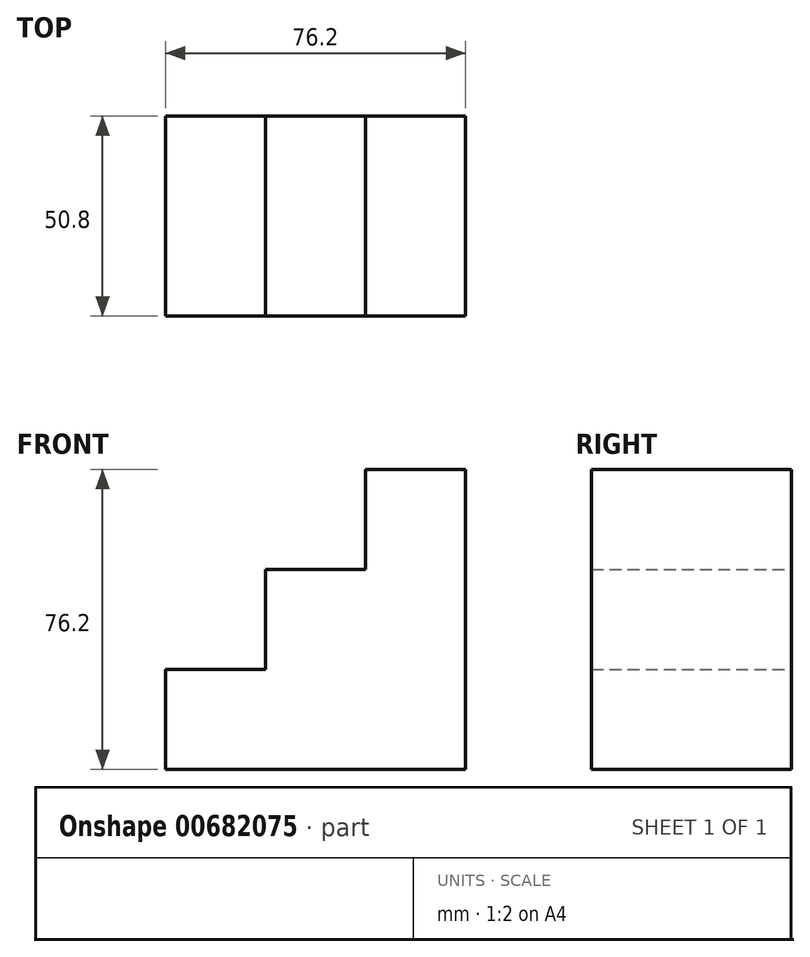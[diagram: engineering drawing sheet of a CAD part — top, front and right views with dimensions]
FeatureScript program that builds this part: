
annotation { "Feature Type Name" : "Feature", "Feature Type Description" : "" }
export const myFeature = defineFeature(function(context is Context, id is Id, definition is map)
    precondition{}
    {
        {
            var Q0;
            Q0=qCreatedBy(makeId("Front.planeOp"),FACE);
            var sketch = newSketch(context, id + "F0", { "sketchPlane" : qUnion([Q0])});
            skLineSegment(sketch, "E0", {"start": v(0, -14.8) * mm, "end": v(76.2, -14.8) * mm});
            skLineSegment(sketch, "E1", {"start": v(76.2, -14.8) * mm, "end": v(76.2, 61.4) * mm});
            skLineSegment(sketch, "E2", {"start": v(76.2, 61.4) * mm, "end": v(50.8, 61.4) * mm});
            skLineSegment(sketch, "E3", {"start": v(50.8, 61.4) * mm, "end": v(50.8, 36) * mm});
            skLineSegment(sketch, "E4", {"start": v(50.8, 36) * mm, "end": v(25.4, 36) * mm});
            skLineSegment(sketch, "E5", {"start": v(25.4, 36) * mm, "end": v(25.4, 10.6) * mm});
            skLineSegment(sketch, "E6", {"start": v(25.4, 10.6) * mm, "end": v(0, 10.6) * mm});
            skLineSegment(sketch, "E7", {"start": v(0, 10.6) * mm, "end": v(0, -14.8) * mm});
            skSolve(sketch);
        }
        {
            var Q0;
            Q0 = qSketchRegion(id + "F0", true);
            extrude(context, id + "F1", {"entities" : qUnion([Q0]), "depth" : 50.8 * mm, "offsetDistance" : 25.4 * mm});
        }
    });
